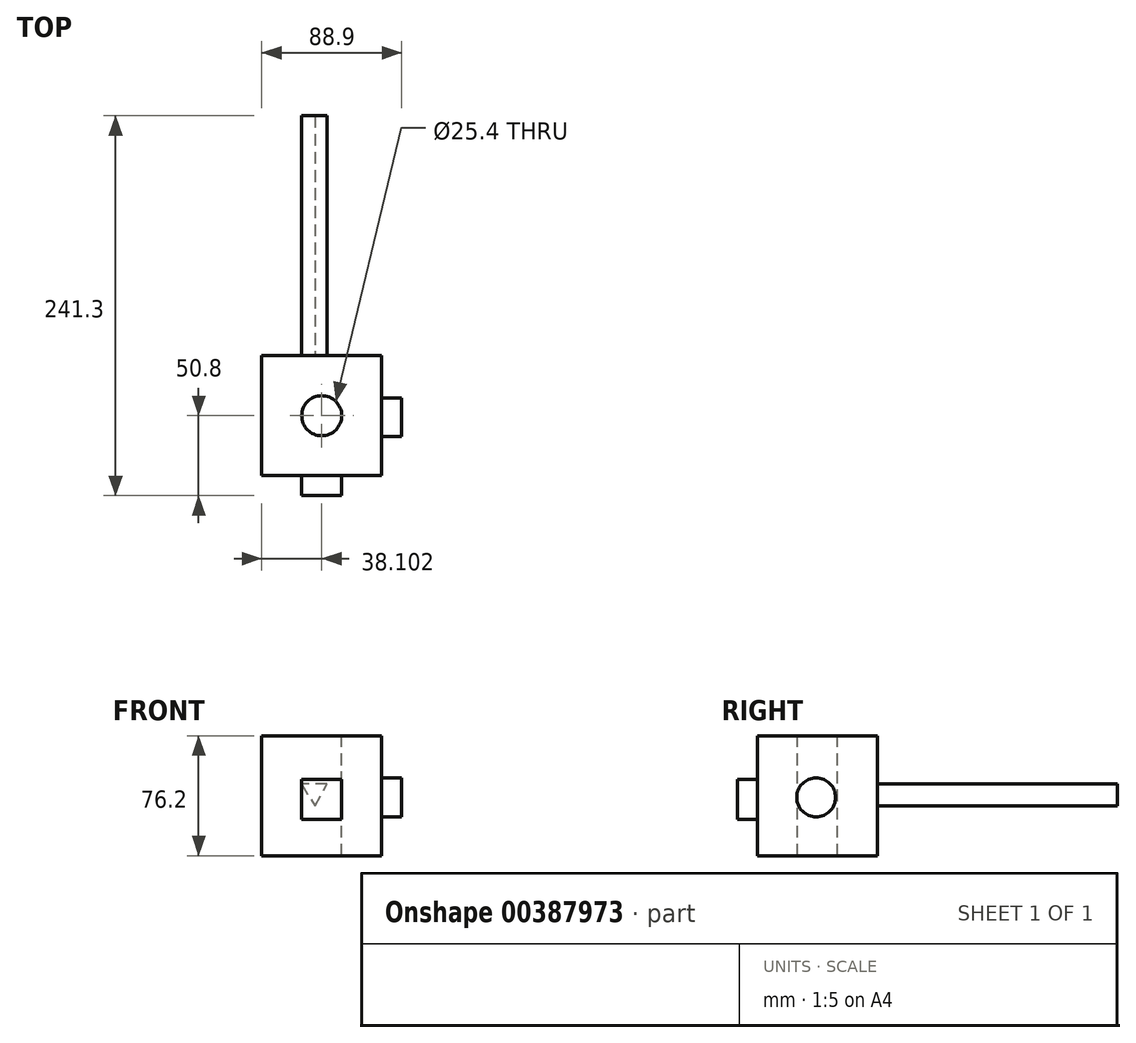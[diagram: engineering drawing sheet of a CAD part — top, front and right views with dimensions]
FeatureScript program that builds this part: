
annotation { "Feature Type Name" : "Feature", "Feature Type Description" : "" }
export const myFeature = defineFeature(function(context is Context, id is Id, definition is map)
    precondition{}
    {
        {
            var Q0;
            Q0=qCreatedBy(makeId("Front.planeOp"),FACE);
            var sketch = newSketch(context, id + "F0", { "sketchPlane" : qUnion([Q0])});
            skLineSegment(sketch, "E0.bottom", {"start": v(-15.8, 27.77) * mm, "end": v(60.4, 27.77) * mm});
            skLineSegment(sketch, "E0.top", {"start": v(-15.8, -48.43) * mm, "end": v(60.4, -48.43) * mm});
            skLineSegment(sketch, "E0.left", {"start": v(-15.8, 27.77) * mm, "end": v(-15.8, -48.43) * mm});
            skLineSegment(sketch, "E0.right", {"start": v(60.4, 27.77) * mm, "end": v(60.4, -48.43) * mm});
            skSolve(sketch);
        }
        {
            var Q0;
            Q0=makeQuery(id+"F0.imprint","IMPRINT",FACE,{"disambiguationData":[TD([[makeQuery(id+"F0.imprint","IMPRINT",EDGE,{"derivedFrom":sQuery(id+"F0.wireOp",EDGE,"E0.bottom")}),-1.0]])]});
            extrude(context, id + "F1", {"entities" : qUnion([Q0]), "depth" : 76.2 * mm});
        }
        {
            var Q0;
            Q0=makeQuery(id+"F1.opExtrude","SWEPT_FACE",FACE,{"disambiguationData":[OSD([sQuery(id+"F0.wireOp",EDGE,"E0.bottom")])]});
            var sketch = newSketch(context, id + "F2", { "sketchPlane" : qUnion([Q0])});
            skPoint(sketch, "E1", {"position": v(22.3, -38.1) * mm});
            skSolve(sketch);
        }
        {
            var Q0;
            Q0=sQuery(id+"F2.wireOp",VERTEX,"E1");
            var Q1;
            Q1=makeQuery(id+"F1.opExtrude","SWEPT_BODY",BODY,{"disambiguationData":[OSD([sQuery(id+"F0.wireOp",EDGE,"E0.bottom"),sQuery(id+"F0.wireOp",EDGE,"E0.top"),sQuery(id+"F0.wireOp",EDGE,"E0.left"),sQuery(id+"F0.wireOp",EDGE,"E0.right")])]});
            hole(context, id + "F3", {"style" : HoleStyle.SIMPLE, "endStyle" : HoleEndStyle.THROUGH, "holeDiameter" : 25.4 * mm, "isTappedThrough" : true, "tappedDepth" : 12.7 * mm, "tapClearance" : 3, "locations" : qUnion([Q0]), "scope" : qUnion([Q1])});
        }
        {
            var Q0;
            Q0=makeQuery(id+"F1.opExtrude","CAP_FACE",FACE,{"disambiguationData":[OSD([sQuery(id+"F0.wireOp",EDGE,"E0.bottom"),sQuery(id+"F0.wireOp",EDGE,"E0.top"),sQuery(id+"F0.wireOp",EDGE,"E0.left"),sQuery(id+"F0.wireOp",EDGE,"E0.right")])],"isStart":false});
            var sketch = newSketch(context, id + "F4", { "sketchPlane" : qUnion([Q0])});
            skLineSegment(sketch, "E2.bottom", {"start": v(9.6, -25.4) * mm, "end": v(35, -25.4) * mm});
            skLineSegment(sketch, "E2.top", {"start": v(9.6, 0) * mm, "end": v(35, 0) * mm});
            skLineSegment(sketch, "E2.left", {"start": v(9.6, -25.4) * mm, "end": v(9.6, 0) * mm});
            skLineSegment(sketch, "E2.right", {"start": v(35, -25.4) * mm, "end": v(35, 0) * mm});
            skSolve(sketch);
        }
        {
            var Q0;
            Q0=makeQuery(id+"F4.imprint","IMPRINT",FACE,{"disambiguationData":[TD([[makeQuery(id+"F4.imprint","IMPRINT",EDGE,{"derivedFrom":sQuery(id+"F4.wireOp",EDGE,"E2.bottom")}),1.0]])]});
            extrude(context, id + "F5", {"entities" : qUnion([Q0]), "operationType" : NewBodyOperationType.ADD, "depth" : 12.7 * mm});
        }
        {
            var Q0;
            Q0=makeQuery(id+"F1.opExtrude","SWEPT_FACE",FACE,{"disambiguationData":[OSD([sQuery(id+"F0.wireOp",EDGE,"E0.right")])]});
            var sketch = newSketch(context, id + "F6", { "sketchPlane" : qUnion([Q0])});
            skCircle(sketch, "E3", {"center": v(-39.05, -11.38) * mm, "radius": 12.33 * mm});
            skSolve(sketch);
        }
        {
            var Q0;
            Q0=makeQuery(id+"F6.imprint","IMPRINT",FACE,{"disambiguationData":[TD([[makeQuery(id+"F6.imprint","IMPRINT",EDGE,{"derivedFrom":sQuery(id+"F6.wireOp",EDGE,"E3")}),1.0]])]});
            extrude(context, id + "F7", {"entities" : qUnion([Q0]), "operationType" : NewBodyOperationType.ADD, "depth" : 12.7 * mm});
        }
        {
            var Q0;
            Q0=makeQuery(id+"F1.opExtrude","CAP_FACE",FACE,{"disambiguationData":[OSD([sQuery(id+"F0.wireOp",EDGE,"E0.bottom"),sQuery(id+"F0.wireOp",EDGE,"E0.top"),sQuery(id+"F0.wireOp",EDGE,"E0.left"),sQuery(id+"F0.wireOp",EDGE,"E0.right")])],"isStart":true});
            var sketch = newSketch(context, id + "F8", { "sketchPlane" : qUnion([Q0])});
            skCircle(sketch, "E4.cCircle", {"center": v(-17.75, -7.49) * mm, "radius": 9.4 * mm, "construction": true});
            skLineSegment(sketch, "E4.0", {"start": v(-25.8, -2.65) * mm, "end": v(-9.53, -2.93) * mm});
            skLineSegment(sketch, "E4.1", {"start": v(-9.53, -2.93) * mm, "end": v(-17.9, -16.88) * mm});
            skLineSegment(sketch, "E4.2", {"start": v(-17.9, -16.88) * mm, "end": v(-25.8, -2.65) * mm});
            skSolve(sketch);
        }
        {
            var Q0;
            Q0=makeQuery(id+"F8.imprint","IMPRINT",FACE,{"disambiguationData":[TD([[makeQuery(id+"F8.imprint","IMPRINT",EDGE,{"derivedFrom":sQuery(id+"F8.wireOp",EDGE,"E4.0")}),-1.0]])]});
            extrude(context, id + "F9", {"entities" : qUnion([Q0]), "operationType" : NewBodyOperationType.ADD, "depth" : 152.4 * mm});
        }
    });
